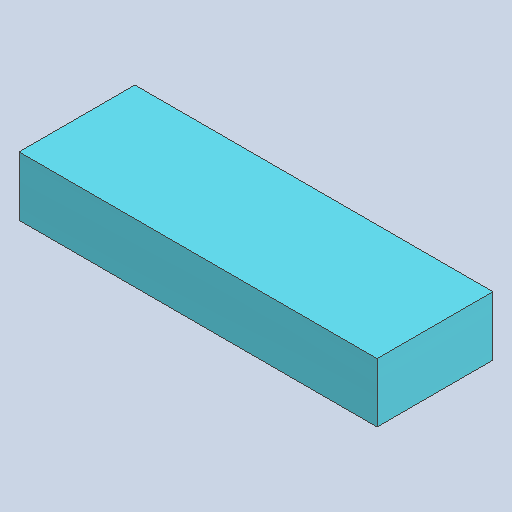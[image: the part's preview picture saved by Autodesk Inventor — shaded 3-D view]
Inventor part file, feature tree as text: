
AUTODESK INVENTOR PART (.ipt)
format: ipt  version: 2025.2 (Build 292293000, 293)  size: 89,088 bytes
history: native  units: mm
features: extrude x1, sketch x1
ambient origin geometry x8: Origin, YZ Plane, XZ Plane, XY Plane, X Axis, Y Axis, Z Axis, Center Point
bodies: Solid1 (feature_tree)
feature tree (2):
  extrude  "Extrusion1"  Depth=44.0mm
  sketch  "Sketch1"  dims[d0=136.0mm d1=44.0mm d2=22.5mm d3=0.0mm]
